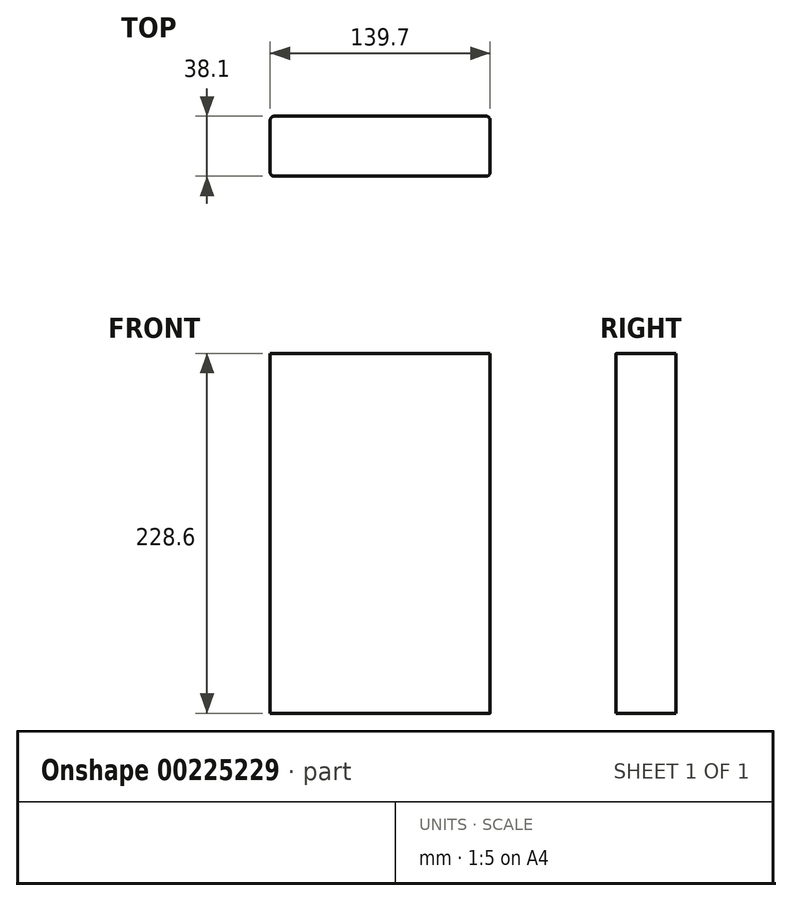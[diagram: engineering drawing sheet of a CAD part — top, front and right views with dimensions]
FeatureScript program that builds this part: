
annotation { "Feature Type Name" : "Feature", "Feature Type Description" : "" }
export const myFeature = defineFeature(function(context is Context, id is Id, definition is map)
    precondition{}
    {
        {
            var Q0;
            Q0=qCreatedBy(makeId("Front.planeOp"),FACE);
            var sketch = newSketch(context, id + "F0", { "sketchPlane" : qUnion([Q0])});
            skLineSegment(sketch, "E0.bottom", {"start": v(0, 0) * mm, "end": v(139.7, 0) * mm});
            skLineSegment(sketch, "E0.top", {"start": v(0, 228.6) * mm, "end": v(139.7, 228.6) * mm});
            skLineSegment(sketch, "E0.left", {"start": v(0, 0) * mm, "end": v(0, 228.6) * mm});
            skLineSegment(sketch, "E0.right", {"start": v(139.7, 0) * mm, "end": v(139.7, 228.6) * mm});
            skSolve(sketch);
        }
        {
            var Q0;
            Q0=makeQuery(id+"F0.imprint","IMPRINT",FACE,{"disambiguationData":[TD([[makeQuery(id+"F0.imprint","IMPRINT",EDGE,{"derivedFrom":sQuery(id+"F0.wireOp",EDGE,"E0.bottom")}),1.0]])]});
            extrude(context, id + "F1", {"entities" : qUnion([Q0]), "depth" : 38.1 * mm});
        }
        {
            var Q0;
            Q0=makeQuery(id+"F1.opExtrude","CAP_EDGE",EDGE,{"disambiguationData":[OSD([sQuery(id+"F0.wireOp",EDGE,"E0.left")])],"isStart":false});
            var Q1;
            Q1=makeQuery(id+"F1.opExtrude","CAP_EDGE",EDGE,{"disambiguationData":[OSD([sQuery(id+"F0.wireOp",EDGE,"E0.right")])],"isStart":false});
            var Q2;
            Q2=makeQuery(id+"F1.opExtrude","CAP_EDGE",EDGE,{"disambiguationData":[OSD([sQuery(id+"F0.wireOp",EDGE,"E0.right")])],"isStart":true});
            var Q3;
            Q3=makeQuery(id+"F1.opExtrude","CAP_EDGE",EDGE,{"disambiguationData":[OSD([sQuery(id+"F0.wireOp",EDGE,"E0.left")])],"isStart":true});
            fillet(context, id + "F2", {"entities" : qUnion([Q0, Q1, Q2, Q3]), "radius" : 2.54 * mm, "tangentPropagation" : true, "allowEdgeOverflow" : false});
        }
    });
